# Revit family: NBS_PineappleContracts_OffcTbls_RynoDiningTable
name_source: partatom
category: Furniture
revit_build: Autodesk Revit 2017 (Build: 20171027_0315(x64)
units: mm (PartAtom-declared; Revit-internal decimal feet)

## family parameters
Always vertical = Yes
Cut with Voids When Loaded = No
Room Calculation Point = No
Shared = No
Work Plane-Based = No

## types (2) — shared parameters
AssetType = Movable
BottomLeg Width = 558 mm
Category = Pr_40_50_21_60:Office tables
ColourOptions = blaze orange, vegas yellow, icon purple, epic blue, moonwalk grey, thunder grey, cool green, lime green, black, granite
Description = Polyethylene activity table
DurationUnit = year
ExposedEdges = Rounded, grey polyethylene edging
Feet = Stainless steel glides
Finish = Anti-microbial, wipe-clean surface with excellent chemical resistance
FrameSupports = Cruciform base design
Functions = Dining room
IfcExportAs = IfcFurnishingElementType
IfcExportType = TABLE
IsBuiltIn = No
Manufacturer = www.pineapplecontracts.com
ManufacturerName = Pineapple Contracts
ManufacturerURL = www.pineapplecontracts.com
Material = Polyethylene
NBSCertification = www.nationalbimlibrary.com/cert/g0nre2pm
NBSDescription = Office tables
NBSReference = 45-35-20/340
NominalHeight = 760 mm
NominalLength = 1235 mm  [stored 4.05184 ft]
NominalWidth = 1235 mm  [stored 4.05184 ft]
NumberOfChairs = 4
ProductInformation = www.pineapplecontracts.com/userfiles/file/RYNO-brochure.pdf
Shape = Circular
Size = 1235 x 1235 x 750 mm
StrengthAndStability = Level 3
TableMaterial = NBS_Concept
TopLegWidth = 479 mm
Uniclass2015Code = Pr_40_50_21_60
Uniclass2015Title = Office tables
Uniclass2015Version = Products v1.13
Version = 6
WarrantyDescription = Guarantee against manufacturing faults
WarrantyDurationParts = 7
WarrantyDurationUnit = year
Weight = 90 kg
zero-valued in all types: NominalDepth, WallThickness, WorksurfaceArea

## per-type parameters (varying)
| type | ModelNumber | ModelReference | Name | TableTop |
| NBS_PineappleContracts_OfficeTables_RynoActivityTable | ARYT-202 | Ryno Activity Table | OfficeTables_RynoActivityTable_PineappleContracts | Flat laminate |
| NBS_PineappleContracts_OfficeTables_RynoDiningTable | ARYT-002 | Ryno Dining Table | OfficeTables_RynoDiningTable_PineappleContracts | Moulded laminate with divided areas |

note: column(s) folded — value = type name in every type: BIMObjectName

note: [stored X ft] marks values corroborated as IEEE doubles in the binary element streams (Revit-internal decimal feet)

## geometry (parser evidence)
native form markers: Sweep x2
no freeform markers — native parametric forms only
